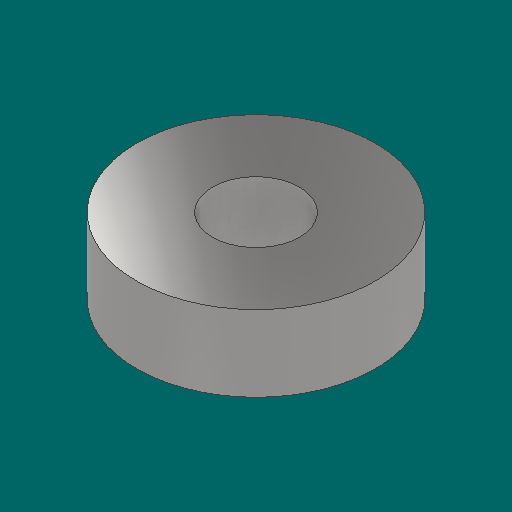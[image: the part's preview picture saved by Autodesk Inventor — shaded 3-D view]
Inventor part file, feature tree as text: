
AUTODESK INVENTOR PART (.ipt)
format: ipt  version: 2023.1 (Build 271208000, 208)  size: 107,520 bytes
history: native  units: in
note: dims shown in document units (in); Inventor stores cm internally (conversion verified against a paired STEP export)
features: other x3, sketch x1
ambient origin geometry x8: Origin, YZ Plane, XZ Plane, XY Plane, X Axis, Y Axis, Z Axis, Center Point
bodies: Solid1 (feature_tree)
feature tree (4):
  other  "608bearing.ipt"
  other  "Solid1::608bearing.ipt"
  other  "TaggingFeature1"
  sketch  "Sketch1"  dims[d0=0.3937in]
